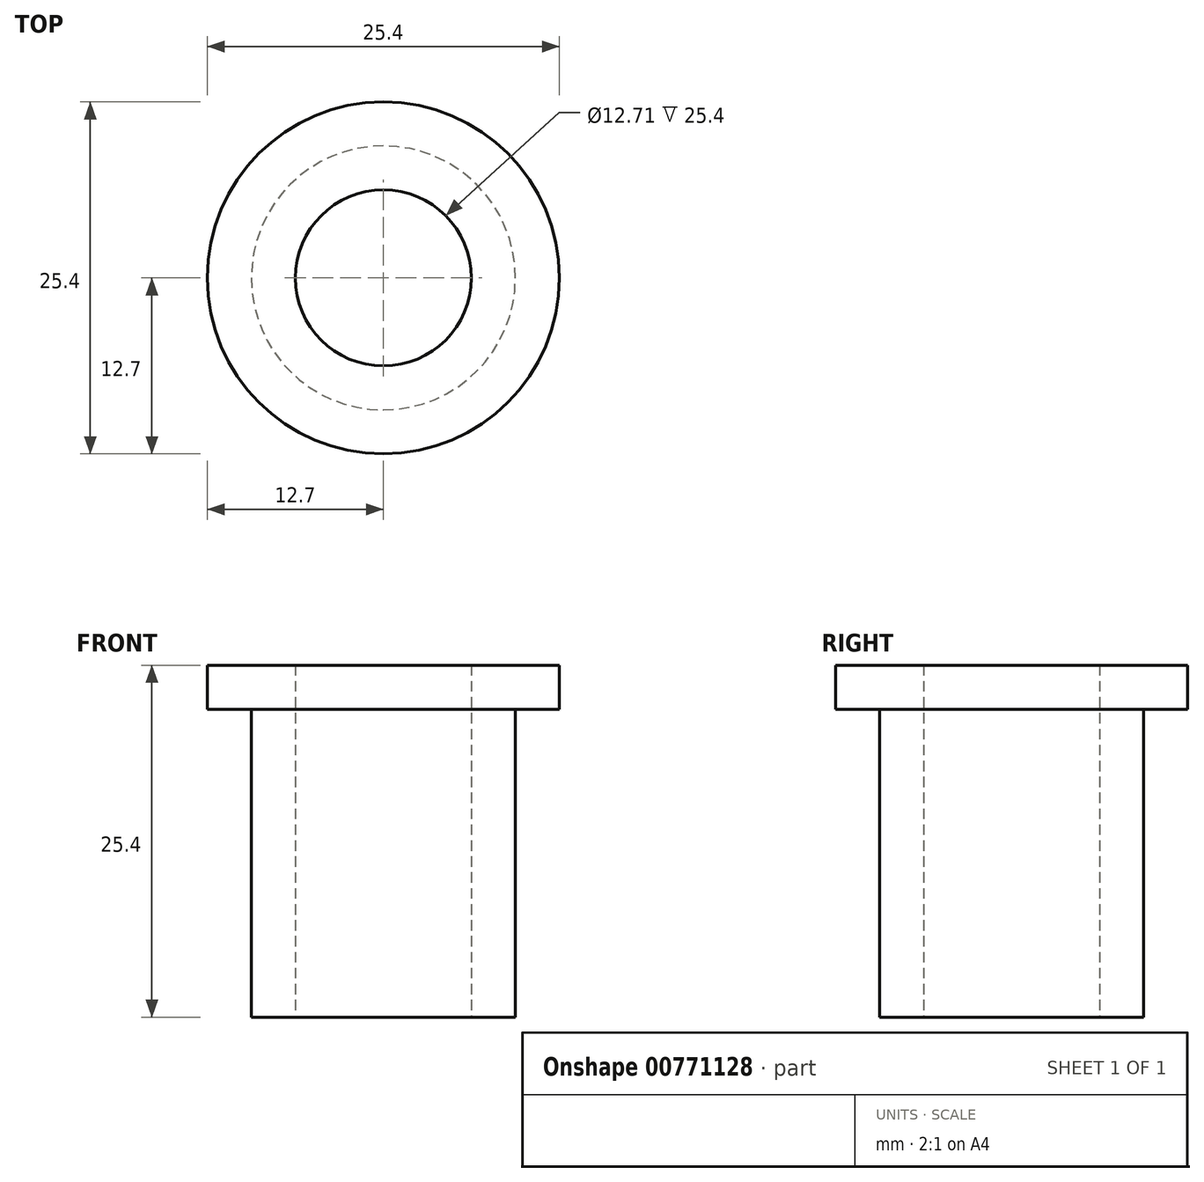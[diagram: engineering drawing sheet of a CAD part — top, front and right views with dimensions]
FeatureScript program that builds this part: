
annotation { "Feature Type Name" : "Feature", "Feature Type Description" : "" }
export const myFeature = defineFeature(function(context is Context, id is Id, definition is map)
    precondition{}
    {
        {
            var Q0;
            Q0=qCreatedBy(makeId("Front.planeOp"),FACE);
            var sketch = newSketch(context, id + "F0", { "sketchPlane" : qUnion([Q0])});
            skLineSegment(sketch, "E0", {"start": v(6.35, 25.4) * mm, "end": v(12.7, 25.4) * mm});
            skLineSegment(sketch, "E1", {"start": v(6.35, 25.4) * mm, "end": v(6.35, 0) * mm});
            skLineSegment(sketch, "E2", {"start": v(6.35, 0) * mm, "end": v(9.52, 0) * mm});
            skLineSegment(sketch, "E3", {"start": v(9.53, 0) * mm, "end": v(9.53, 22.23) * mm});
            skLineSegment(sketch, "E4", {"start": v(9.52, 22.23) * mm, "end": v(12.7, 22.23) * mm});
            skLineSegment(sketch, "E5", {"start": v(12.7, 22.23) * mm, "end": v(12.7, 25.4) * mm});
            skLineSegment(sketch, "E6", {"start": v(0, 0) * mm, "end": v(0, 60.47) * mm, "construction": true});
            skSolve(sketch);
        }
        {
            var Q0;
            Q0 = qSketchRegion(id + "F0", true);
            var Q1;
            Q1=sQuery(id+"F0.wireOp",EDGE,"E6");
            revolve(context, id + "F1", {"surfaceOperationType" : NewSurfaceOperationType.NEW, "entities" : qUnion([Q0]), "axis" : qUnion([Q1]), "revolveType" : RevolveType.FULL});
        }
    });
